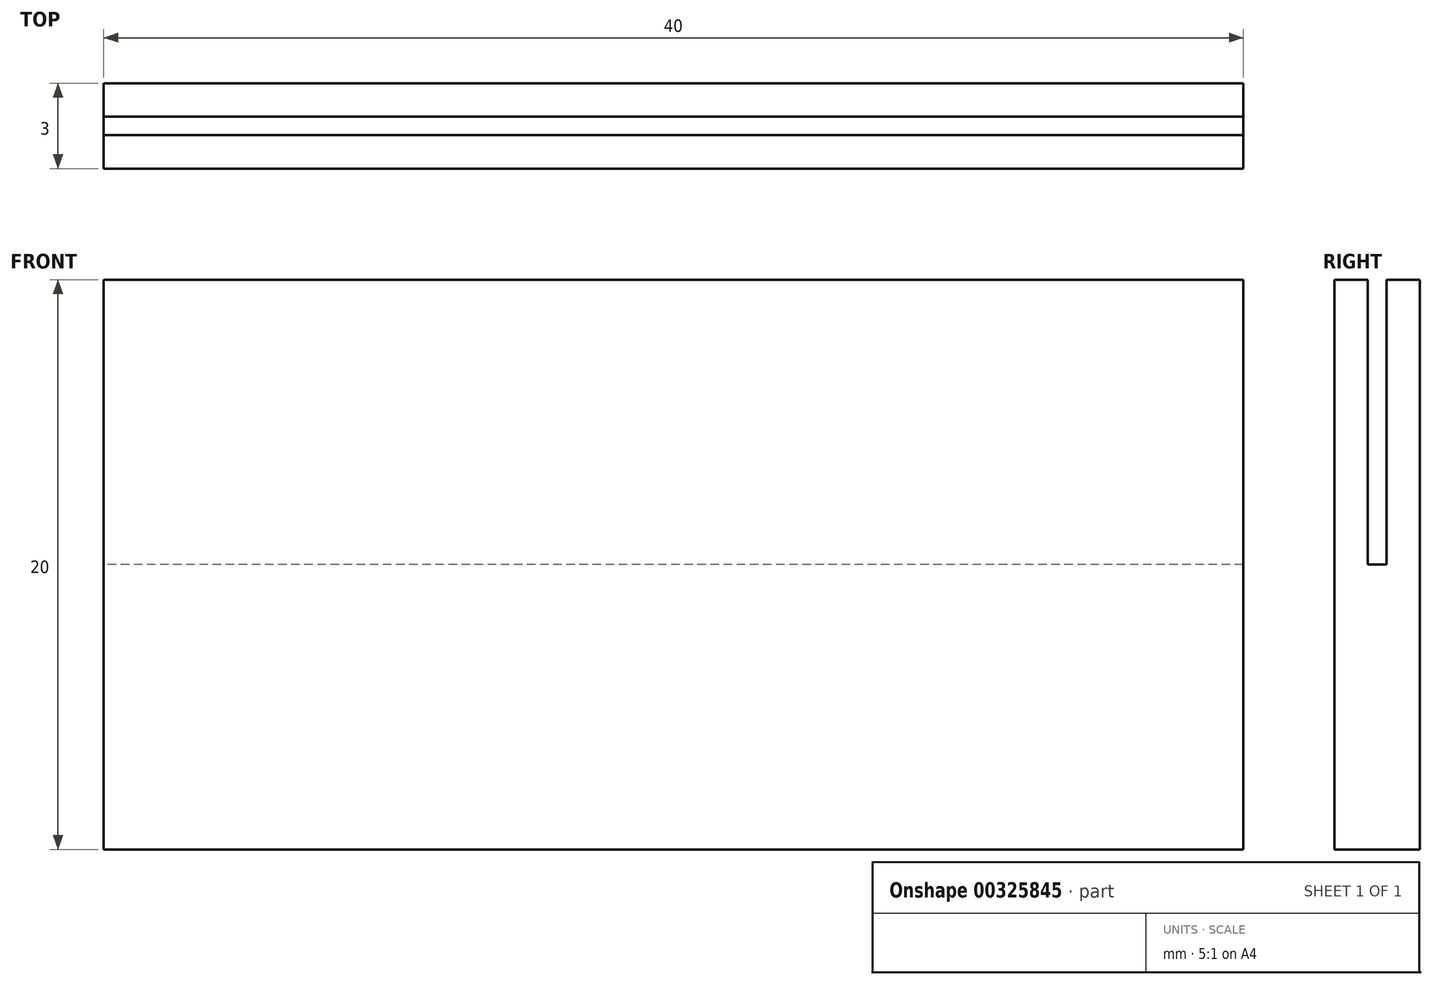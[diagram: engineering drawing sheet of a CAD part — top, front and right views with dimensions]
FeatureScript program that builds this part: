
annotation { "Feature Type Name" : "Feature", "Feature Type Description" : "" }
export const myFeature = defineFeature(function(context is Context, id is Id, definition is map)
    precondition{}
    {
        {
            var Q0;
            Q0=qCreatedBy(makeId("Top.planeOp"),FACE);
            var sketch = newSketch(context, id + "F0", { "sketchPlane" : qUnion([Q0])});
            skLineSegment(sketch, "E0.bottom", {"start": v(20, -1.5) * mm, "end": v(-20, -1.5) * mm});
            skLineSegment(sketch, "E0.top", {"start": v(20, 1.5) * mm, "end": v(-20, 1.5) * mm});
            skLineSegment(sketch, "E0.left", {"start": v(20, -1.5) * mm, "end": v(20, 1.5) * mm});
            skLineSegment(sketch, "E0.right", {"start": v(-20, -1.5) * mm, "end": v(-20, 1.5) * mm});
            skPoint(sketch, "E0.middle", {"position": v(0, 0) * mm});
            skLineSegment(sketch, "E1.bottom", {"start": v(20, -0.33) * mm, "end": v(-20, -0.33) * mm});
            skLineSegment(sketch, "E1.top", {"start": v(20, 0.33) * mm, "end": v(-20, 0.33) * mm});
            skLineSegment(sketch, "E1.left", {"start": v(20, -0.33) * mm, "end": v(20, 0.33) * mm});
            skLineSegment(sketch, "E1.right", {"start": v(-20, -0.33) * mm, "end": v(-20, 0.33) * mm});
            skSolve(sketch);
        }
        {
            var Q0;
            Q0 = qSketchRegion(id + "F0", true);
            extrude(context, id + "F1", {"entities" : qUnion([Q0]), "oppositeDirection" : true, "depth" : 20 * mm});
        }
        {
            var Q0;
            Q0=makeQuery(id+"F0.imprint","IMPRINT",FACE,{"disambiguationData":[TD([[makeQuery(id+"F0.imprint","IMPRINT",EDGE,{"derivedFrom":sQuery(id+"F0.wireOp",EDGE,"E1.bottom")}),-1.0]])]});
            extrude(context, id + "F2", {"entities" : qUnion([Q0]), "operationType" : NewBodyOperationType.REMOVE, "oppositeDirection" : true, "depth" : 10 * mm});
        }
    });
